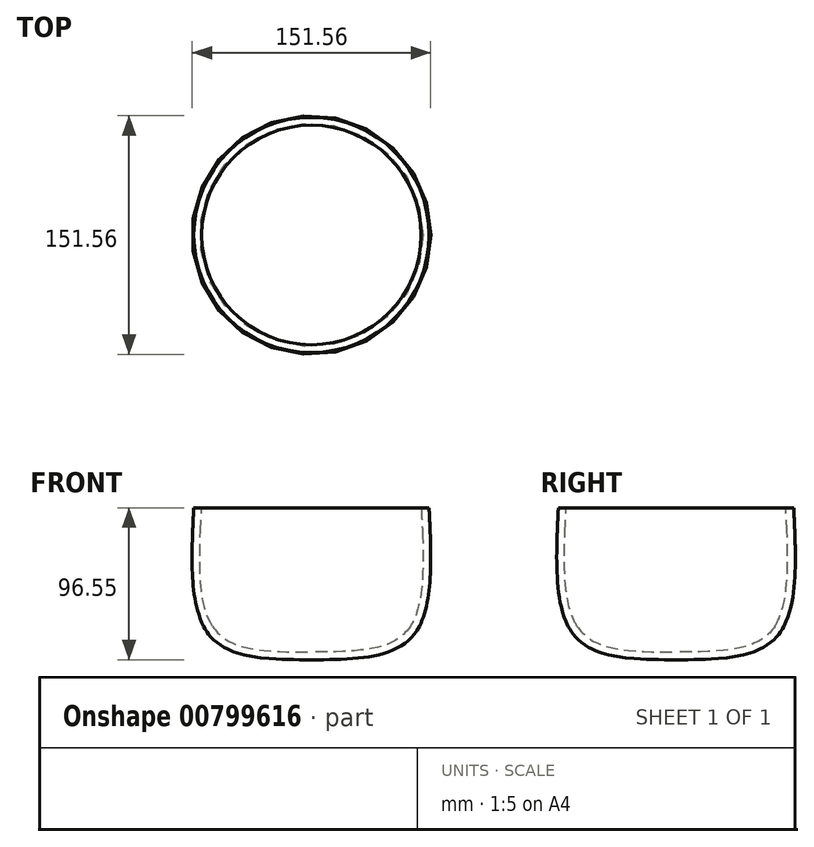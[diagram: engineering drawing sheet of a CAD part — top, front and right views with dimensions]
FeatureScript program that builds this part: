
annotation { "Feature Type Name" : "Feature", "Feature Type Description" : "" }
export const myFeature = defineFeature(function(context is Context, id is Id, definition is map)
    precondition{}
    {
        {
            var Q0;
            Q0=qCreatedBy(makeId("Front.planeOp"),FACE);
            var sketch = newSketch(context, id + "F0", { "sketchPlane" : qUnion([Q0])});
            skLineSegment(sketch, "E0", {"start": v(0, 65.29) * mm, "end": v(0, -51.06) * mm});
            skFitSpline(sketch, "E1", {"points": [v(74.73, 56.63) * mm, v(63.59, -25.68) * mm, v(0, -39.92) * mm], "startDerivative": vector(9.32, -188.33) * mm, "endDerivative": vector(-162.24, -0.97) * mm});
            skFitSpline(sketch, "E2.0", {"points": [v(69.73, 56.38) * mm, v(70.12, 48.53) * mm, v(70.7, 36.82) * mm, v(70.84, 22.05) * mm, v(70.48, 11.58) * mm, v(69.52, 1.91) * mm, v(67.83, -6.73) * mm, v(65.75, -12.9) * mm, v(63.66, -17.15) * mm, v(62.17, -19.5) * mm, v(60.88, -21.2) * mm, v(59.85, -22.38) * mm, v(58.76, -23.5) * mm, v(57.2, -24.88) * mm, v(55.06, -26.46) * mm, v(51.22, -28.69) * mm, v(45.66, -30.92) * mm, v(37.9, -32.8) * mm, v(29.23, -33.97) * mm, v(19.9, -34.6) * mm, v(10.08, -34.86) * mm, v(3.35, -34.9) * mm, v(-0.03, -34.92) * mm]});
            skLineSegment(sketch, "E3", {"start": v(69.73, 56.38) * mm, "end": v(74.73, 56.63) * mm});
            skLineSegment(sketch, "E4", {"start": v(32, 41.44) * mm, "end": v(98.6, 41.44) * mm});
            skLineSegment(sketch, "E5", {"start": v(113.6, 26.44) * mm, "end": v(113.6, -3.56) * mm});
            skLineSegment(sketch, "E6", {"start": v(98.6, -18.56) * mm, "end": v(32.95, -18.56) * mm});
            skPoint(sketch, "E7.visualSharp", {"position": v(113.6, 41.44) * mm});
            skArc(sketch, "E7.filletArc", {"start": v(113.6, 26.44) * mm, "mid": v(109.2, 37.04) * mm, "end": v(98.6, 41.44) * mm});
            skPoint(sketch, "E8.visualSharp", {"position": v(113.6, -18.56) * mm});
            skArc(sketch, "E8.filletArc", {"start": v(98.6, -18.56) * mm, "mid": v(109.2, -14.17) * mm, "end": v(113.6, -3.56) * mm});
            skSolve(sketch);
        }
        {
            var Q0;
            {var subQ0=sQuery(id+"F0.wireOp",EDGE,"E1");Q0=makeQuery(id+"F0.imprint","IMPRINT",FACE,{"disambiguationData":[TD([[makeQuery(id+"F0.imprint","IMPRINT",EDGE,{"derivedFrom":subQ0}),-1.0]])]});}
            var Q1;
            Q1=sQuery(id+"F0.wireOp",EDGE,"E0");
            revolve(context, id + "F1", {"surfaceOperationType" : NewSurfaceOperationType.NEW, "entities" : qUnion([Q0]), "axis" : qUnion([Q1]), "revolveType" : RevolveType.FULL});
        }
        {
            var Q0;
            Q0=sQuery(id+"F0.wireOp",EDGE,"E4");
            var Q1;
            Q1=sQuery(id+"F0.wireOp",VERTEX,"E4.start");
            cPlane(context, id + "F2", {"entities" : qUnion([Q0, Q1]), "cplaneType" : CPlaneType.LINE_POINT, "offset" : 25 * mm, "width" : 150 * mm, "height" : 150 * mm});
        }
    });
